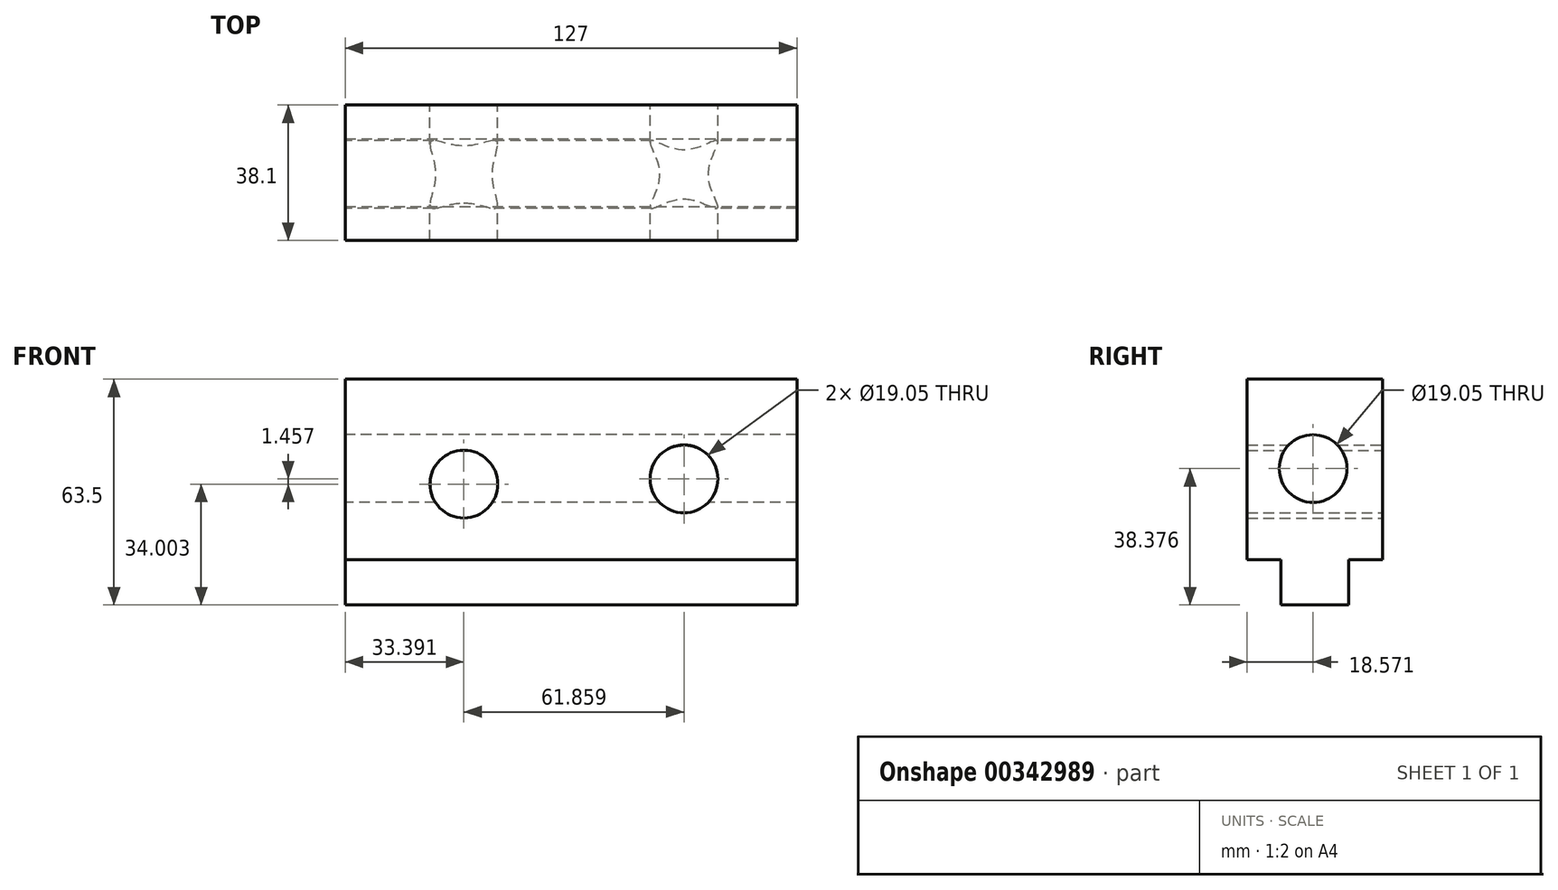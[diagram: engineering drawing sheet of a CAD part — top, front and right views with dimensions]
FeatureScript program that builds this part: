
annotation { "Feature Type Name" : "Feature", "Feature Type Description" : "" }
export const myFeature = defineFeature(function(context is Context, id is Id, definition is map)
    precondition{}
    {
        {
            var Q0;
            Q0=qCreatedBy(makeId("Front.planeOp"),FACE);
            var sketch = newSketch(context, id + "F0", { "sketchPlane" : qUnion([Q0])});
            skLineSegment(sketch, "E0", {"start": v(-63.97, -30.36) * mm, "end": v(63.03, -30.36) * mm});
            skLineSegment(sketch, "E1", {"start": v(63.03, -30.36) * mm, "end": v(63.03, 33.14) * mm});
            skLineSegment(sketch, "E2", {"start": v(63.03, 33.14) * mm, "end": v(-63.97, 33.14) * mm});
            skLineSegment(sketch, "E3", {"start": v(-63.97, 33.14) * mm, "end": v(-63.97, -30.36) * mm});
            skCircle(sketch, "E4", {"center": v(31.28, 5.1) * mm, "radius": 9.53 * mm});
            skCircle(sketch, "E5", {"center": v(-30.58, 3.64) * mm, "radius": 9.53 * mm});
            skLineSegment(sketch, "E6", {"start": v(-63.97, -17.66) * mm, "end": v(63.03, -17.66) * mm});
            skSolve(sketch);
        }
        {
            var Q0;
            {var subQ1=sQuery(id+"F0.wireOp",EDGE,"E2");Q0=makeQuery(id+"F0.imprint","IMPRINT",FACE,{"disambiguationData":[TD([[makeQuery(id+"F0.imprint","IMPRINT",EDGE,{"derivedFrom":subQ1}),1.0]])]});}
            extrude(context, id + "F1", {"entities" : qUnion([Q0]), "depth" : 38.1 * mm});
        }
        {
            var Q0;
            {var subQ0=sQuery(id+"F0.wireOp",EDGE,"E0");Q0=makeQuery(id+"F0.imprint","IMPRINT",FACE,{"disambiguationData":[TD([[makeQuery(id+"F0.imprint","IMPRINT",EDGE,{"derivedFrom":subQ0}),1.0]])]});}
            extrude(context, id + "F2", {"entities" : qUnion([Q0]), "operationType" : NewBodyOperationType.ADD, "depth" : 28.57 * mm, "hasSecondDirection" : true, "secondDirectionOppositeDirection" : false, "secondDirectionDepth" : 9.52 * mm});
        }
        {
            var Q0;
            Q0=qCreatedBy(makeId("Right.planeOp"),FACE);
            var sketch = newSketch(context, id + "F3", { "sketchPlane" : qUnion([Q0])});
            skCircle(sketch, "E7", {"center": v(-19.53, 8.02) * mm, "radius": 9.53 * mm});
            skSolve(sketch);
        }
        {
            var Q0;
            Q0=makeQuery(id+"F3.imprint","IMPRINT",FACE,{"disambiguationData":[TD([[makeQuery(id+"F3.imprint","IMPRINT",EDGE,{"derivedFrom":sQuery(id+"F3.wireOp",EDGE,"E7")}),1.0]])]});
            extrude(context, id + "F4", {"entities" : qUnion([Q0]), "operationType" : NewBodyOperationType.REMOVE, "depth" : 74.93 * mm, "hasSecondDirection" : true, "secondDirectionOppositeDirection" : true, "secondDirectionDepth" : 90.68 * mm});
        }
    });
